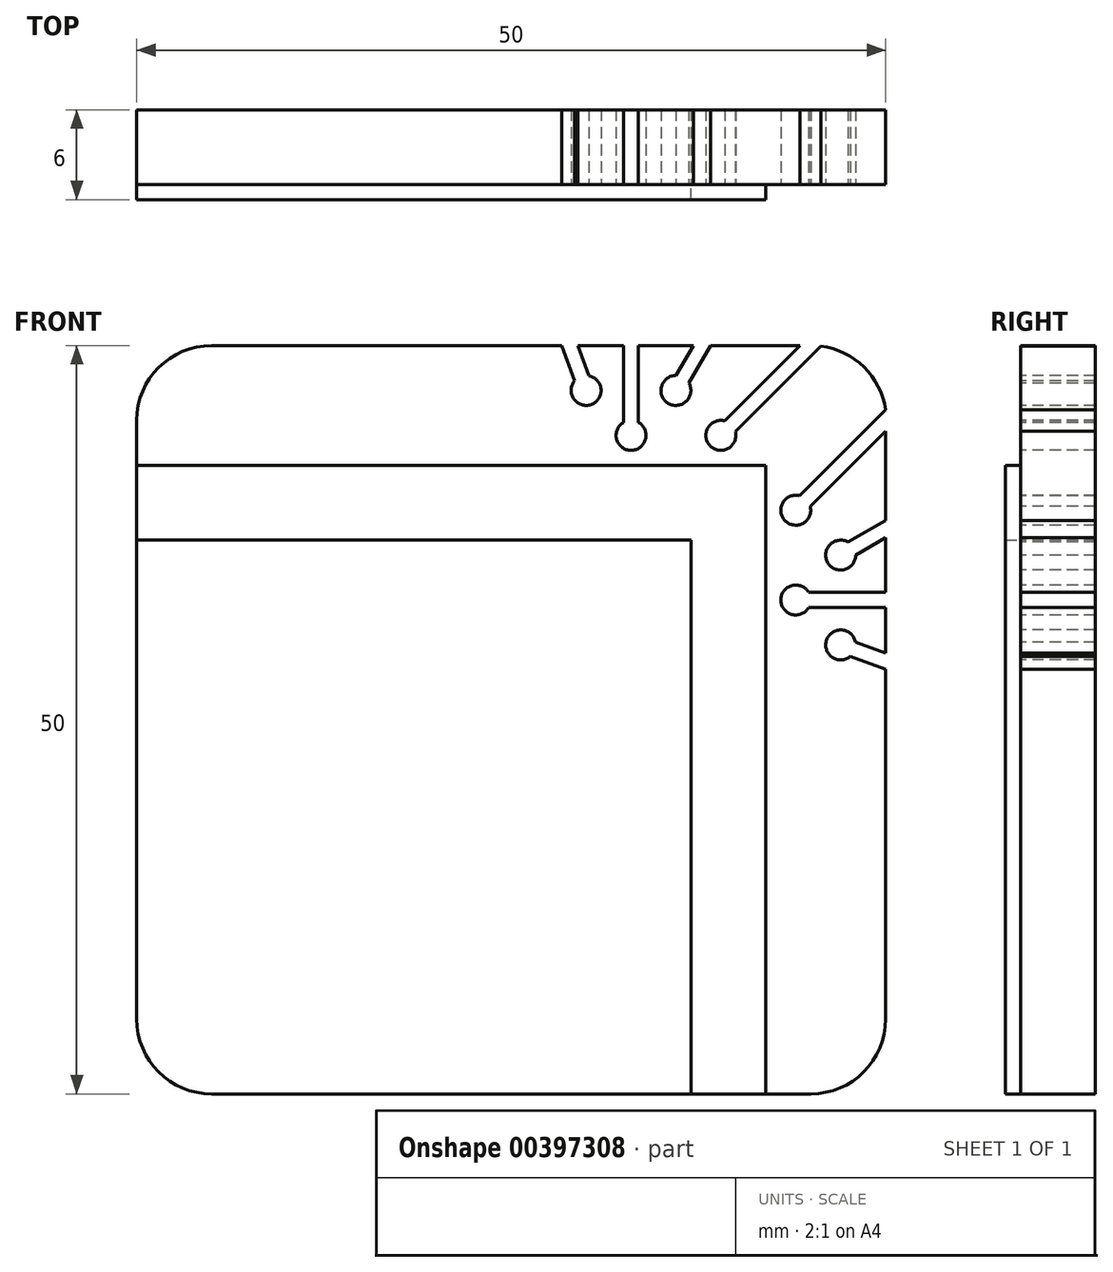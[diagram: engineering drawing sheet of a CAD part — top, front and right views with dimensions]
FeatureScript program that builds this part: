
annotation { "Feature Type Name" : "Feature", "Feature Type Description" : "" }
export const myFeature = defineFeature(function(context is Context, id is Id, definition is map)
    precondition{}
    {
        {
            var Q0;
            Q0=qCreatedBy(makeId("Front.planeOp"),FACE);
            var sketch = newSketch(context, id + "F0", { "sketchPlane" : qUnion([Q0])});
            skLineSegment(sketch, "E0.bottom", {"start": v(0, 0) * mm, "end": v(50, 0) * mm});
            skLineSegment(sketch, "E0.top", {"start": v(0, 50) * mm, "end": v(50, 50) * mm});
            skLineSegment(sketch, "E0.left", {"start": v(0, 0) * mm, "end": v(0, 50) * mm});
            skLineSegment(sketch, "E0.right", {"start": v(50, 0) * mm, "end": v(50, 50) * mm});
            skLineSegment(sketch, "E1", {"start": v(0, 0) * mm, "end": v(50, 50) * mm});
            skLineSegment(sketch, "E2", {"start": v(0, 42) * mm, "end": v(42, 42) * mm});
            skLineSegment(sketch, "E3", {"start": v(0, 37) * mm, "end": v(37, 37) * mm});
            skLineSegment(sketch, "E4", {"start": v(0, 47) * mm, "end": v(50, 47) * mm, "construction": true});
            skLineSegment(sketch, "E5", {"start": v(0, 44) * mm, "end": v(50, 44) * mm, "construction": true});
            skLineSegment(sketch, "E6", {"start": v(42, 42) * mm, "end": v(42, 50) * mm, "construction": true});
            skLineSegment(sketch, "E7", {"start": v(33.11, 42) * mm, "end": v(37.73, 50) * mm, "construction": true});
            skLineSegment(sketch, "E8", {"start": v(33, 42) * mm, "end": v(33, 50) * mm, "construction": true});
            skLineSegment(sketch, "E9", {"start": v(31.82, 42) * mm, "end": v(28.9, 50) * mm, "construction": true});
            skPoint(sketch, "E10", {"position": v(36, 47) * mm});
            skPoint(sketch, "E11", {"position": v(33, 44) * mm});
            skPoint(sketch, "E12", {"position": v(30, 47) * mm});
            skLineSegment(sketch, "E13", {"start": v(37, 42) * mm, "end": v(45, 50) * mm, "construction": true});
            skPoint(sketch, "E14", {"position": v(39, 44) * mm});
            skSolve(sketch);
        }
        {
            var Q0;
            Q0=qCreatedBy(makeId("Front.planeOp"),FACE);
            var sketch = newSketch(context, id + "F1", { "sketchPlane" : qUnion([Q0])});
            skCircle(sketch, "E15", {"center": v(39, 44) * mm, "radius": 1 * mm});
            skCircle(sketch, "E16", {"center": v(36, 47) * mm, "radius": 1 * mm});
            skCircle(sketch, "E17", {"center": v(30, 47) * mm, "radius": 1 * mm});
            skCircle(sketch, "E18", {"center": v(33, 44) * mm, "radius": 1 * mm});
            skLineSegment(sketch, "E19", {"start": v(45.7, 50) * mm, "end": v(39.97, 44.26) * mm});
            skLineSegment(sketch, "E20.MirrorCS", {"start": v(44.3, 50) * mm, "end": v(39.26, 44.97) * mm});
            skLineSegment(sketch, "E21", {"start": v(36.87, 47.5) * mm, "end": v(38.3, 50) * mm});
            skLineSegment(sketch, "E22", {"start": v(30.17, 47.98) * mm, "end": v(29.44, 50) * mm});
            skLineSegment(sketch, "E23", {"start": v(33.5, 44.87) * mm, "end": v(33.5, 50) * mm});
            skLineSegment(sketch, "E24.MirrorCS", {"start": v(32.5, 44.87) * mm, "end": v(32.5, 50) * mm});
            skLineSegment(sketch, "E25.MirrorCS", {"start": v(36, 48) * mm, "end": v(37.15, 50) * mm});
            skLineSegment(sketch, "E26.MirrorCS", {"start": v(29.23, 47.64) * mm, "end": v(28.38, 50) * mm});
            skLineSegment(sketch, "E27", {"start": v(28.38, 50) * mm, "end": v(29.44, 50) * mm});
            skLineSegment(sketch, "E28", {"start": v(32.5, 50) * mm, "end": v(33.5, 50) * mm});
            skLineSegment(sketch, "E29", {"start": v(37.15, 50) * mm, "end": v(38.3, 50) * mm});
            skLineSegment(sketch, "E30", {"start": v(44.3, 50) * mm, "end": v(45.7, 50) * mm});
            skSolve(sketch);
        }
        {
            var Q0;
            {var subQ3=sQuery(id+"F0.wireOp",EDGE,"E3");Q0=makeQuery(id+"F0.imprint","IMPRINT",FACE,{"disambiguationData":[TD([[makeQuery(id+"F0.imprint","IMPRINT",EDGE,{"derivedFrom":subQ3}),-1.0]])]});}
            var Q1;
            {var subQ0=sQuery(id+"F0.wireOp",EDGE,"E2");Q1=makeQuery(id+"F0.imprint","IMPRINT",FACE,{"disambiguationData":[TD([[makeQuery(id+"F0.imprint","IMPRINT",EDGE,{"derivedFrom":subQ0}),-1.0]])]});}
            var Q2;
            {var subQ0=sQuery(id+"F0.wireOp",EDGE,"E0.top");Q2=makeQuery(id+"F0.imprint","IMPRINT",FACE,{"disambiguationData":[TD([[makeQuery(id+"F0.imprint","IMPRINT",EDGE,{"derivedFrom":subQ0}),-1.0]])]});}
            extrude(context, id + "F2", {"entities" : qUnion([Q0, Q1, Q2]), "oppositeDirection" : true, "depth" : 5 * mm});
        }
        {
            var Q0;
            {var subQ0=sQuery(id+"F0.wireOp",EDGE,"E2");Q0=makeQuery(id+"F0.imprint","IMPRINT",FACE,{"disambiguationData":[TD([[makeQuery(id+"F0.imprint","IMPRINT",EDGE,{"derivedFrom":subQ0}),-1.0]])]});}
            extrude(context, id + "F3", {"entities" : qUnion([Q0]), "depth" : 1 * mm});
        }
        {
            var Q0;
            {var subQ0=sQuery(id+"F1.wireOp",EDGE,"E17");var subQ1=makeQuery(id+"F1.imprint","INTERSECT",VERTEX,{"derivedFrom":[subQ0,sQuery(id+"F1.wireOp",EDGE,"E22")]});Q0=makeQuery(id+"F1.imprint","IMPRINT",FACE,{"disambiguationData":[TD([[makeQuery(id+"F1.imprint","IMPRINT",EDGE,{"disambiguationData":[TD([[subQ1,-1.0]])],"derivedFrom":subQ0}),1.0]])]});}
            var Q1;
            {var subQ0=sQuery(id+"F1.wireOp",EDGE,"E22");Q1=makeQuery(id+"F1.imprint","IMPRINT",FACE,{"disambiguationData":[TD([[makeQuery(id+"F1.imprint","IMPRINT",EDGE,{"derivedFrom":subQ0}),1.0]])]});}
            var Q2;
            {var subQ0=sQuery(id+"F1.wireOp",EDGE,"E18");var subQ1=makeQuery(id+"F1.imprint","INTERSECT",VERTEX,{"derivedFrom":[subQ0,sQuery(id+"F1.wireOp",EDGE,"E23")]});Q2=makeQuery(id+"F1.imprint","IMPRINT",FACE,{"disambiguationData":[TD([[makeQuery(id+"F1.imprint","IMPRINT",EDGE,{"disambiguationData":[TD([[subQ1,-1.0]])],"derivedFrom":subQ0}),1.0]])]});}
            var Q3;
            {var subQ0=sQuery(id+"F1.wireOp",EDGE,"E23");Q3=makeQuery(id+"F1.imprint","IMPRINT",FACE,{"disambiguationData":[TD([[makeQuery(id+"F1.imprint","IMPRINT",EDGE,{"derivedFrom":subQ0}),1.0]])]});}
            var Q4;
            {var subQ0=sQuery(id+"F1.wireOp",EDGE,"E16");var subQ1=makeQuery(id+"F1.imprint","INTERSECT",VERTEX,{"derivedFrom":[subQ0,sQuery(id+"F1.wireOp",EDGE,"E21")]});Q4=makeQuery(id+"F1.imprint","IMPRINT",FACE,{"disambiguationData":[TD([[makeQuery(id+"F1.imprint","IMPRINT",EDGE,{"disambiguationData":[TD([[subQ1,-1.0]])],"derivedFrom":subQ0}),1.0]])]});}
            var Q5;
            {var subQ0=sQuery(id+"F1.wireOp",EDGE,"E15");var subQ1=makeQuery(id+"F1.imprint","INTERSECT",VERTEX,{"derivedFrom":[subQ0,sQuery(id+"F1.wireOp",EDGE,"E19")]});Q5=makeQuery(id+"F1.imprint","IMPRINT",FACE,{"disambiguationData":[TD([[makeQuery(id+"F1.imprint","IMPRINT",EDGE,{"disambiguationData":[TD([[subQ1,-1.0]])],"derivedFrom":subQ0}),1.0]])]});}
            var Q6;
            {var subQ0=sQuery(id+"F1.wireOp",EDGE,"E19");Q6=makeQuery(id+"F1.imprint","IMPRINT",FACE,{"disambiguationData":[TD([[makeQuery(id+"F1.imprint","IMPRINT",EDGE,{"derivedFrom":subQ0}),-1.0]])]});}
            var Q7;
            {var subQ0=sQuery(id+"F1.wireOp",EDGE,"E21");Q7=makeQuery(id+"F1.imprint","IMPRINT",FACE,{"disambiguationData":[TD([[makeQuery(id+"F1.imprint","IMPRINT",EDGE,{"derivedFrom":subQ0}),1.0]])]});}
            extrude(context, id + "F4", {"entities" : qUnion([Q0, Q1, Q2, Q3, Q4, Q5, Q6, Q7]), "operationType" : NewBodyOperationType.REMOVE, "endBound" : BoundingType.UP_TO_NEXT, "oppositeDirection" : true, "depth" : 25 * mm});
        }
        {
            var Q0;
            Q0=makeQuery(id+"F2.opExtrude","SWEPT_BODY",BODY,{"disambiguationData":[OSD([sQuery(id+"F0.wireOp",EDGE,"E0.top"),sQuery(id+"F0.wireOp",EDGE,"E0.left"),sQuery(id+"F0.wireOp",EDGE,"E1")])]});
            var Q1;
            Q1=makeQuery(id+"F2.opExtrude","SWEPT_FACE",FACE,{"disambiguationData":[OSD([sQuery(id+"F0.wireOp",EDGE,"E1")])]});
            mirror(context, id + "F5", {"operationType" : NewBodyOperationType.ADD, "entities" : qUnion([Q0]), "mirrorPlane" : qUnion([Q1])});
        }
        {
            var Q0;
            Q0=makeQuery(id+"F3.opExtrude","SWEPT_BODY",BODY,{"disambiguationData":[OSD([sQuery(id+"F0.wireOp",EDGE,"E0.left"),sQuery(id+"F0.wireOp",EDGE,"E1"),sQuery(id+"F0.wireOp",EDGE,"E2"),sQuery(id+"F0.wireOp",EDGE,"E3")])]});
            var Q1;
            Q1=makeQuery(id+"F3.opExtrude","SWEPT_FACE",FACE,{"disambiguationData":[OSD([sQuery(id+"F0.wireOp",EDGE,"E1")])]});
            mirror(context, id + "F6", {"operationType" : NewBodyOperationType.ADD, "entities" : qUnion([Q0]), "mirrorPlane" : qUnion([Q1])});
        }
        {
            var Q0;
            {var subQ0=makeQuery(id+"F2.opExtrude","SWEPT_EDGE",EDGE,{"disambiguationData":[OSD([sQuery(id+"F0.wireOp",EDGE,"E0.top"),sQuery(id+"F0.wireOp",EDGE,"E0.right"),sQuery(id+"F0.wireOp",EDGE,"E1")])]});Q0=makeQuery(id+"F5.boolean.opBoolean","MERGE",EDGE,{"derivedFrom":[subQ0,makeQuery(id+"F5.opPattern","COPY",EDGE,{"derivedFrom":subQ0,"instanceName":"1"})]});}
            var Q1;
            {var subQ0=makeQuery(id+"F2.opExtrude","SWEPT_EDGE",EDGE,{"disambiguationData":[OSD([sQuery(id+"F0.wireOp",EDGE,"E0.bottom"),sQuery(id+"F0.wireOp",EDGE,"E0.left"),sQuery(id+"F0.wireOp",EDGE,"E1")])]});Q1=makeQuery(id+"F5.boolean.opBoolean","MERGE",EDGE,{"derivedFrom":[subQ0,makeQuery(id+"F5.opPattern","COPY",EDGE,{"derivedFrom":subQ0,"instanceName":"1"})]});}
            var Q2;
            Q2=makeQuery(id+"F5.opPattern","COPY",EDGE,{"derivedFrom":makeQuery(id+"F2.opExtrude","SWEPT_EDGE",EDGE,{"disambiguationData":[OSD([sQuery(id+"F0.wireOp",EDGE,"E0.top"),sQuery(id+"F0.wireOp",EDGE,"E0.left")])]}),"instanceName":"1"});
            var Q3;
            Q3=makeQuery(id+"F2.opExtrude","SWEPT_EDGE",EDGE,{"disambiguationData":[OSD([sQuery(id+"F0.wireOp",EDGE,"E0.top"),sQuery(id+"F0.wireOp",EDGE,"E0.left")])]});
            fillet(context, id + "F7", {"entities" : qUnion([Q0, Q1, Q2, Q3]), "radius" : 5 * mm, "tangentPropagation" : true, "allowEdgeOverflow" : false});
        }
    });
